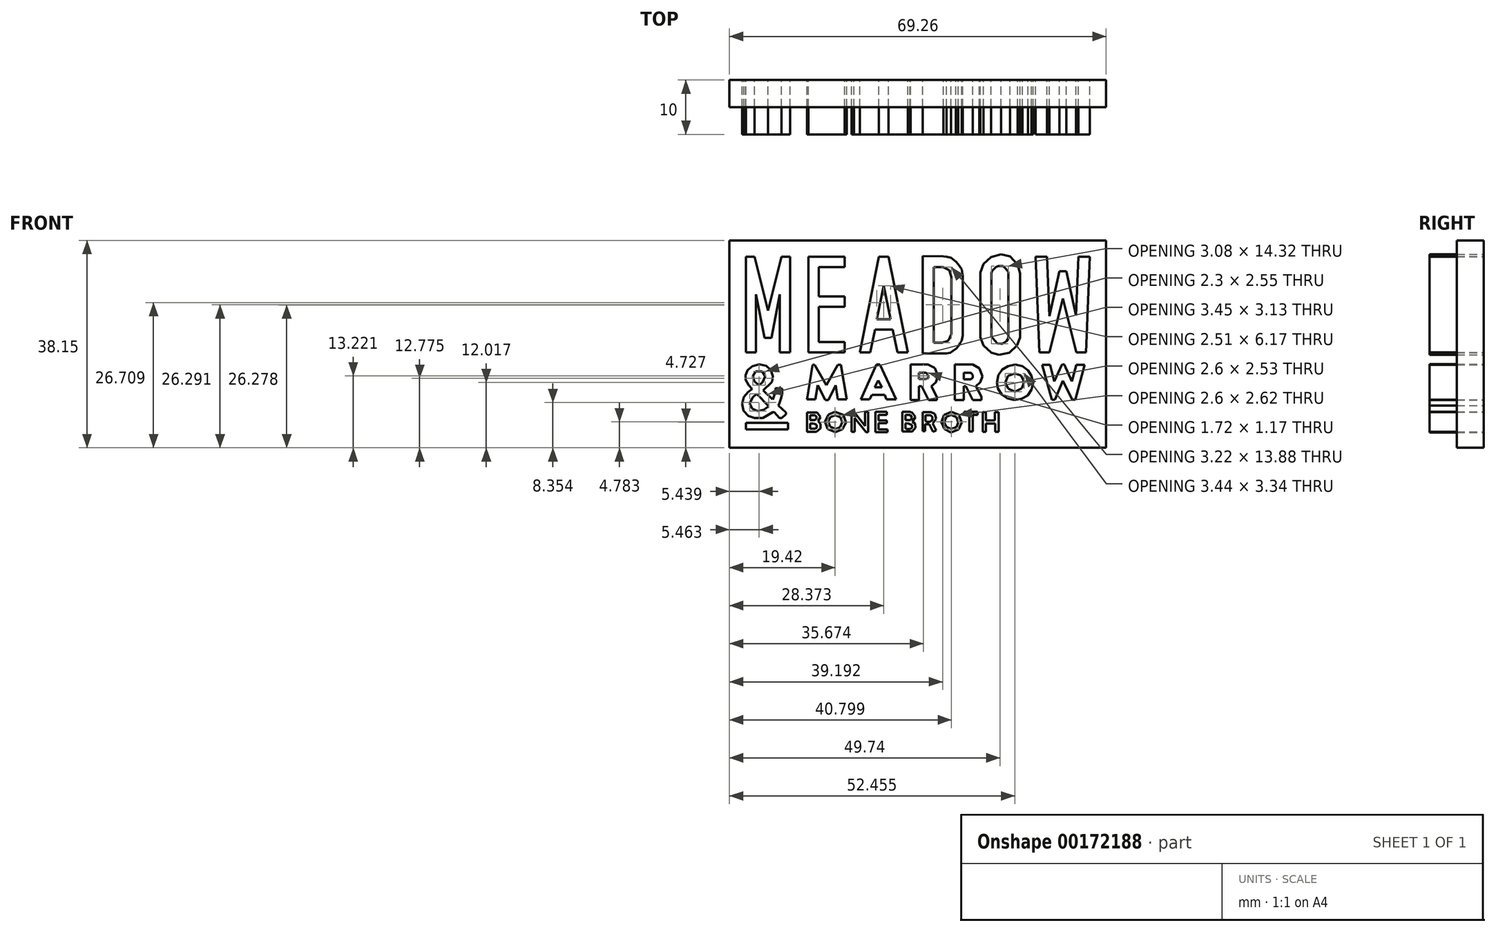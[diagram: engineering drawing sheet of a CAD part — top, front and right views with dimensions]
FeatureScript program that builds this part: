
annotation { "Feature Type Name" : "Feature", "Feature Type Description" : "" }
export const myFeature = defineFeature(function(context is Context, id is Id, definition is map)
    precondition{}
    {
        {
            var Q0;
            Q0=qCreatedBy(makeId("Front.planeOp"),FACE);
            var sketch = newSketch(context, id + "F0", { "sketchPlane" : qUnion([Q0])});
            skLineSegment(sketch, "E0", {"start": v(-7.57, -8.05) * mm, "end": v(-6.9, -6.6) * mm});
            skLineSegment(sketch, "E1", {"start": v(-6.9, -6.6) * mm, "end": v(-6.9, -6.6) * mm});
            skLineSegment(sketch, "E2", {"start": v(-6.9, -6.6) * mm, "end": v(-6.23, -8.05) * mm});
            skLineSegment(sketch, "E3", {"start": v(-6.23, -8.05) * mm, "end": v(-7.57, -8.05) * mm});
            skLineSegment(sketch, "E4", {"start": v(-31.63, -15.97) * mm, "end": v(-23.85, -15.97) * mm});
            skLineSegment(sketch, "E5", {"start": v(-23.85, -15.97) * mm, "end": v(-23.85, -14.73) * mm});
            skLineSegment(sketch, "E6", {"start": v(-23.85, -14.73) * mm, "end": v(-31.63, -14.73) * mm});
            skLineSegment(sketch, "E7", {"start": v(-31.63, -14.73) * mm, "end": v(-31.63, -15.97) * mm});
            skLineSegment(sketch, "E8", {"start": v(-5.38, 15.8) * mm, "end": v(-7.14, 15.8) * mm});
            skLineSegment(sketch, "E9", {"start": v(-7.14, 15.8) * mm, "end": v(-10.66, -1.8) * mm});
            skLineSegment(sketch, "E10", {"start": v(-10.66, -1.8) * mm, "end": v(-8.75, -1.8) * mm});
            skLineSegment(sketch, "E11", {"start": v(-8.75, -1.8) * mm, "end": v(-7.9, 2.38) * mm});
            skLineSegment(sketch, "E12", {"start": v(-7.9, 2.38) * mm, "end": v(-4.62, 2.38) * mm});
            skLineSegment(sketch, "E13", {"start": v(-4.62, 2.38) * mm, "end": v(-3.76, -1.8) * mm});
            skLineSegment(sketch, "E14", {"start": v(-3.76, -1.8) * mm, "end": v(-1.86, -1.8) * mm});
            skLineSegment(sketch, "E15", {"start": v(-1.86, -1.8) * mm, "end": v(-5.38, 15.8) * mm});
            skLineSegment(sketch, "E16", {"start": v(-7.51, 4.28) * mm, "end": v(-6.26, 10.44) * mm});
            skLineSegment(sketch, "E17", {"start": v(-6.26, 10.44) * mm, "end": v(-5, 4.28) * mm});
            skLineSegment(sketch, "E18", {"start": v(-5, 4.28) * mm, "end": v(-7.51, 4.28) * mm});
            skLineSegment(sketch, "E19", {"start": v(29.55, 15.8) * mm, "end": v(29.08, 5) * mm});
            skLineSegment(sketch, "E20", {"start": v(29.08, 5) * mm, "end": v(27.32, 13.16) * mm});
            skLineSegment(sketch, "E21", {"start": v(27.32, 13.16) * mm, "end": v(26.02, 13.16) * mm});
            skLineSegment(sketch, "E22", {"start": v(26.02, 13.16) * mm, "end": v(24.23, 4.9) * mm});
            skLineSegment(sketch, "E23", {"start": v(24.23, 4.9) * mm, "end": v(23.79, 15.8) * mm});
            skLineSegment(sketch, "E24", {"start": v(23.79, 15.8) * mm, "end": v(21.69, 15.8) * mm});
            skLineSegment(sketch, "E25", {"start": v(21.69, 15.8) * mm, "end": v(22.38, -1.79) * mm});
            skLineSegment(sketch, "E26", {"start": v(22.38, -1.79) * mm, "end": v(24.19, -1.79) * mm});
            skLineSegment(sketch, "E27", {"start": v(24.19, -1.79) * mm, "end": v(26.68, 8.1) * mm});
            skLineSegment(sketch, "E28", {"start": v(26.68, 8.1) * mm, "end": v(29.13, -1.79) * mm});
            skLineSegment(sketch, "E29", {"start": v(29.13, -1.79) * mm, "end": v(30.94, -1.79) * mm});
            skLineSegment(sketch, "E30", {"start": v(30.94, -1.79) * mm, "end": v(31.63, 15.8) * mm});
            skLineSegment(sketch, "E31", {"start": v(31.63, 15.8) * mm, "end": v(29.55, 15.8) * mm});
            skLineSegment(sketch, "E32", {"start": v(-13.46, 0.1) * mm, "end": v(-18.21, 0.1) * mm});
            skLineSegment(sketch, "E33", {"start": v(-18.21, 0.1) * mm, "end": v(-18.21, 6.59) * mm});
            skLineSegment(sketch, "E34", {"start": v(-18.21, 6.59) * mm, "end": v(-13.46, 6.59) * mm});
            skLineSegment(sketch, "E35", {"start": v(-13.46, 6.59) * mm, "end": v(-13.46, 8.48) * mm});
            skLineSegment(sketch, "E36", {"start": v(-13.46, 8.48) * mm, "end": v(-18.21, 8.48) * mm});
            skLineSegment(sketch, "E37", {"start": v(-18.21, 8.48) * mm, "end": v(-18.21, 13.9) * mm});
            skLineSegment(sketch, "E38", {"start": v(-18.21, 13.9) * mm, "end": v(-13.46, 13.9) * mm});
            skLineSegment(sketch, "E39", {"start": v(-13.46, 13.9) * mm, "end": v(-13.46, 15.8) * mm});
            skLineSegment(sketch, "E40", {"start": v(-13.46, 15.8) * mm, "end": v(-20.1, 15.8) * mm});
            skLineSegment(sketch, "E41", {"start": v(-20.1, 15.8) * mm, "end": v(-20.1, -1.8) * mm});
            skLineSegment(sketch, "E42", {"start": v(-20.1, -1.8) * mm, "end": v(-13.46, -1.8) * mm});
            skLineSegment(sketch, "E43", {"start": v(-13.46, -1.8) * mm, "end": v(-13.46, 0.1) * mm});
            skLineSegment(sketch, "E44", {"start": v(-27.56, 5.91) * mm, "end": v(-30.01, 15.8) * mm});
            skLineSegment(sketch, "E45", {"start": v(-30.01, 15.8) * mm, "end": v(-31.63, 15.8) * mm});
            skLineSegment(sketch, "E46", {"start": v(-31.63, 15.8) * mm, "end": v(-31.63, -1.8) * mm});
            skLineSegment(sketch, "E47", {"start": v(-31.63, -1.8) * mm, "end": v(-29.74, -1.8) * mm});
            skLineSegment(sketch, "E48", {"start": v(-29.74, -1.8) * mm, "end": v(-29.74, 8.85) * mm});
            skLineSegment(sketch, "E49", {"start": v(-29.74, 8.85) * mm, "end": v(-28.2, 0.84) * mm});
            skLineSegment(sketch, "E50", {"start": v(-28.2, 0.84) * mm, "end": v(-26.9, 0.84) * mm});
            skLineSegment(sketch, "E51", {"start": v(-26.9, 0.84) * mm, "end": v(-25.36, 8.85) * mm});
            skLineSegment(sketch, "E52", {"start": v(-25.36, 8.85) * mm, "end": v(-25.36, -1.8) * mm});
            skLineSegment(sketch, "E53", {"start": v(-25.36, -1.8) * mm, "end": v(-23.47, -1.8) * mm});
            skLineSegment(sketch, "E54", {"start": v(-23.47, -1.8) * mm, "end": v(-23.47, 15.8) * mm});
            skLineSegment(sketch, "E55", {"start": v(-23.47, 15.8) * mm, "end": v(-25.06, 15.8) * mm});
            skLineSegment(sketch, "E56", {"start": v(-25.06, 15.8) * mm, "end": v(-27.56, 5.91) * mm});
            skSolve(sketch);
        }
        {
            var Q0;
            Q0=qCreatedBy(makeId("Front.planeOp"),FACE);
            var sketch = newSketch(context, id + "F1", { "sketchPlane" : qUnion([Q0])});
            skLineSegment(sketch, "E57", {"start": v(0.89, 15.9) * mm, "end": v(0.89, -1.98) * mm});
            skLineSegment(sketch, "E58", {"start": v(0.89, -1.98) * mm, "end": v(5.3, -1.98) * mm});
            skLineSegment(sketch, "E59", {"start": v(5.3, -1.98) * mm, "end": v(5.97, -1.83) * mm});
            skLineSegment(sketch, "E60", {"start": v(5.97, -1.83) * mm, "end": v(6.45, -1.51) * mm});
            skLineSegment(sketch, "E61", {"start": v(6.45, -1.51) * mm, "end": v(7.04, -1.1) * mm});
            skLineSegment(sketch, "E62", {"start": v(7.04, -1.1) * mm, "end": v(7.52, -0.56) * mm});
            skLineSegment(sketch, "E63", {"start": v(7.52, -0.56) * mm, "end": v(7.81, 0) * mm});
            skLineSegment(sketch, "E64", {"start": v(7.81, 0) * mm, "end": v(8.06, 0.36) * mm});
            skLineSegment(sketch, "E65", {"start": v(8.06, 0.36) * mm, "end": v(8.21, 1) * mm});
            skLineSegment(sketch, "E66", {"start": v(8.21, 1) * mm, "end": v(8.29, 1.32) * mm});
            skLineSegment(sketch, "E67", {"start": v(8.29, 1.32) * mm, "end": v(8.29, 12.23) * mm});
            skLineSegment(sketch, "E68", {"start": v(8.29, 12.23) * mm, "end": v(8.1, 13.5) * mm});
            skLineSegment(sketch, "E69", {"start": v(8.1, 13.5) * mm, "end": v(7.45, 14.4) * mm});
            skLineSegment(sketch, "E70", {"start": v(7.45, 14.4) * mm, "end": v(6.99, 14.94) * mm});
            skLineSegment(sketch, "E71", {"start": v(6.99, 14.94) * mm, "end": v(6.1, 15.58) * mm});
            skLineSegment(sketch, "E72", {"start": v(6.1, 15.58) * mm, "end": v(5.3, 15.8) * mm});
            skLineSegment(sketch, "E73", {"start": v(5.3, 15.8) * mm, "end": v(4.74, 15.88) * mm});
            skLineSegment(sketch, "E74", {"start": v(4.74, 15.88) * mm, "end": v(0.89, 15.9) * mm});
            skLineSegment(sketch, "E75", {"start": v(2.95, 13.87) * mm, "end": v(2.95, 0) * mm});
            skLineSegment(sketch, "E76", {"start": v(2.95, 0) * mm, "end": v(4.47, 0) * mm});
            skLineSegment(sketch, "E77", {"start": v(4.47, 0) * mm, "end": v(5.48, 0.3) * mm});
            skLineSegment(sketch, "E78", {"start": v(5.48, 0.3) * mm, "end": v(5.73, 0.54) * mm});
            skLineSegment(sketch, "E79", {"start": v(5.73, 0.54) * mm, "end": v(6.14, 1.46) * mm});
            skLineSegment(sketch, "E80", {"start": v(6.14, 1.46) * mm, "end": v(6.17, 1.54) * mm});
            skLineSegment(sketch, "E81", {"start": v(6.17, 1.54) * mm, "end": v(6.17, 12.02) * mm});
            skLineSegment(sketch, "E82", {"start": v(6.17, 12.02) * mm, "end": v(5.8, 13.32) * mm});
            skLineSegment(sketch, "E83", {"start": v(5.8, 13.32) * mm, "end": v(4.63, 13.88) * mm});
            skLineSegment(sketch, "E84", {"start": v(4.63, 13.88) * mm, "end": v(2.95, 13.87) * mm});
            skLineSegment(sketch, "E85", {"start": v(13.57, 12.8) * mm, "end": v(13.57, 1.13) * mm});
            skLineSegment(sketch, "E86", {"start": v(13.57, 1.13) * mm, "end": v(14.15, 0.34) * mm});
            skLineSegment(sketch, "E87", {"start": v(14.15, 0.34) * mm, "end": v(14.59, -0.14) * mm});
            skLineSegment(sketch, "E88", {"start": v(14.59, -0.14) * mm, "end": v(15.25, -0.23) * mm});
            skLineSegment(sketch, "E89", {"start": v(15.25, -0.23) * mm, "end": v(15.52, -0.23) * mm});
            skLineSegment(sketch, "E90", {"start": v(15.52, -0.23) * mm, "end": v(15.91, 0) * mm});
            skLineSegment(sketch, "E91", {"start": v(15.91, 0) * mm, "end": v(16.35, 0.32) * mm});
            skLineSegment(sketch, "E92", {"start": v(16.35, 0.32) * mm, "end": v(16.65, 0.8) * mm});
            skLineSegment(sketch, "E93", {"start": v(16.65, 0.8) * mm, "end": v(16.65, 1.05) * mm});
            skLineSegment(sketch, "E94", {"start": v(16.65, 1.05) * mm, "end": v(16.65, 13) * mm});
            skLineSegment(sketch, "E95", {"start": v(16.65, 13) * mm, "end": v(16.16, 13.65) * mm});
            skLineSegment(sketch, "E96", {"start": v(16.16, 13.65) * mm, "end": v(15.67, 14.09) * mm});
            skLineSegment(sketch, "E97", {"start": v(15.67, 14.09) * mm, "end": v(14.82, 14.09) * mm});
            skLineSegment(sketch, "E98", {"start": v(14.82, 14.09) * mm, "end": v(14.36, 13.86) * mm});
            skLineSegment(sketch, "E99", {"start": v(14.36, 13.86) * mm, "end": v(13.95, 13.51) * mm});
            skLineSegment(sketch, "E100", {"start": v(13.95, 13.51) * mm, "end": v(13.67, 13.22) * mm});
            skLineSegment(sketch, "E101", {"start": v(13.67, 13.22) * mm, "end": v(13.57, 12.8) * mm});
            skLineSegment(sketch, "E102", {"start": v(11.5, 12.88) * mm, "end": v(11.5, 1.03) * mm});
            skLineSegment(sketch, "E103", {"start": v(11.5, 1.03) * mm, "end": v(12.07, -0.53) * mm});
            skLineSegment(sketch, "E104", {"start": v(12.07, -0.53) * mm, "end": v(13.53, -1.87) * mm});
            skLineSegment(sketch, "E105", {"start": v(13.53, -1.87) * mm, "end": v(14.96, -2.25) * mm});
            skLineSegment(sketch, "E106", {"start": v(14.96, -2.25) * mm, "end": v(16.81, -1.86) * mm});
            skLineSegment(sketch, "E107", {"start": v(16.81, -1.86) * mm, "end": v(18.23, -0.53) * mm});
            skLineSegment(sketch, "E108", {"start": v(18.23, -0.53) * mm, "end": v(18.82, 0.93) * mm});
            skLineSegment(sketch, "E109", {"start": v(18.82, 0.93) * mm, "end": v(18.82, 12.77) * mm});
            skLineSegment(sketch, "E110", {"start": v(18.82, 12.77) * mm, "end": v(18.37, 14.36) * mm});
            skLineSegment(sketch, "E111", {"start": v(18.37, 14.36) * mm, "end": v(16.98, 15.88) * mm});
            skLineSegment(sketch, "E112", {"start": v(16.98, 15.88) * mm, "end": v(15.33, 16.22) * mm});
            skLineSegment(sketch, "E113", {"start": v(15.33, 16.22) * mm, "end": v(13.48, 15.74) * mm});
            skLineSegment(sketch, "E114", {"start": v(13.48, 15.74) * mm, "end": v(12.07, 14.46) * mm});
            skLineSegment(sketch, "E115", {"start": v(12.07, 14.46) * mm, "end": v(11.5, 12.88) * mm});
            skLineSegment(sketch, "E116", {"start": v(-29.27, -7.85) * mm, "end": v(-28.57, -7.34) * mm});
            skLineSegment(sketch, "E117", {"start": v(-28.57, -7.34) * mm, "end": v(-28.04, -6.15) * mm});
            skLineSegment(sketch, "E118", {"start": v(-28.04, -6.15) * mm, "end": v(-28.61, -5.3) * mm});
            skLineSegment(sketch, "E119", {"start": v(-28.61, -5.3) * mm, "end": v(-29.8, -5.3) * mm});
            skLineSegment(sketch, "E120", {"start": v(-29.8, -5.3) * mm, "end": v(-30.34, -6.2) * mm});
            skLineSegment(sketch, "E121", {"start": v(-30.34, -6.2) * mm, "end": v(-30.06, -7.08) * mm});
            skLineSegment(sketch, "E122", {"start": v(-30.06, -7.08) * mm, "end": v(-29.27, -7.85) * mm});
            skLineSegment(sketch, "E123", {"start": v(-26.73, -10.45) * mm, "end": v(-28.4, -8.8) * mm});
            skLineSegment(sketch, "E124", {"start": v(-28.4, -8.8) * mm, "end": v(-26.92, -7.3) * mm});
            skLineSegment(sketch, "E125", {"start": v(-26.92, -7.3) * mm, "end": v(-26.77, -7.1) * mm});
            skLineSegment(sketch, "E126", {"start": v(-26.77, -7.1) * mm, "end": v(-26.64, -6.18) * mm});
            skLineSegment(sketch, "E127", {"start": v(-26.64, -6.18) * mm, "end": v(-27.04, -5.05) * mm});
            skLineSegment(sketch, "E128", {"start": v(-27.04, -5.05) * mm, "end": v(-27.85, -4.3) * mm});
            skLineSegment(sketch, "E129", {"start": v(-27.85, -4.3) * mm, "end": v(-28.98, -4.02) * mm});
            skLineSegment(sketch, "E130", {"start": v(-28.98, -4.02) * mm, "end": v(-29.27, -4.02) * mm});
            skLineSegment(sketch, "E131", {"start": v(-29.27, -4.02) * mm, "end": v(-30.42, -4.31) * mm});
            skLineSegment(sketch, "E132", {"start": v(-30.42, -4.31) * mm, "end": v(-31.27, -5.05) * mm});
            skLineSegment(sketch, "E133", {"start": v(-31.27, -5.05) * mm, "end": v(-31.67, -6) * mm});
            skLineSegment(sketch, "E134", {"start": v(-31.67, -6) * mm, "end": v(-31.67, -6.83) * mm});
            skLineSegment(sketch, "E135", {"start": v(-31.67, -6.83) * mm, "end": v(-31.1, -7.85) * mm});
            skLineSegment(sketch, "E136", {"start": v(-31.1, -7.85) * mm, "end": v(-30.45, -8.53) * mm});
            skLineSegment(sketch, "E137", {"start": v(-30.45, -8.53) * mm, "end": v(-31.22, -9.1) * mm});
            skLineSegment(sketch, "E138", {"start": v(-31.22, -9.1) * mm, "end": v(-31.99, -9.96) * mm});
            skLineSegment(sketch, "E139", {"start": v(-31.99, -9.96) * mm, "end": v(-32.29, -11.25) * mm});
            skLineSegment(sketch, "E140", {"start": v(-32.29, -11.25) * mm, "end": v(-32.04, -12.5) * mm});
            skLineSegment(sketch, "E141", {"start": v(-32.04, -12.5) * mm, "end": v(-31.18, -13.46) * mm});
            skLineSegment(sketch, "E142", {"start": v(-31.18, -13.46) * mm, "end": v(-30, -13.87) * mm});
            skLineSegment(sketch, "E143", {"start": v(-30, -13.87) * mm, "end": v(-28.53, -13.87) * mm});
            skLineSegment(sketch, "E144", {"start": v(-28.53, -13.87) * mm, "end": v(-26.66, -12.8) * mm});
            skLineSegment(sketch, "E145", {"start": v(-26.66, -12.8) * mm, "end": v(-26.42, -12.8) * mm});
            skLineSegment(sketch, "E146", {"start": v(-26.42, -12.8) * mm, "end": v(-25.45, -13.85) * mm});
            skLineSegment(sketch, "E147", {"start": v(-25.45, -13.85) * mm, "end": v(-24.98, -13.85) * mm});
            skLineSegment(sketch, "E148", {"start": v(-24.98, -13.85) * mm, "end": v(-24.27, -13.17) * mm});
            skLineSegment(sketch, "E149", {"start": v(-24.27, -13.17) * mm, "end": v(-24.27, -12.82) * mm});
            skLineSegment(sketch, "E150", {"start": v(-24.27, -12.82) * mm, "end": v(-25.61, -11.57) * mm});
            skLineSegment(sketch, "E151", {"start": v(-25.61, -11.57) * mm, "end": v(-25.45, -11.1) * mm});
            skLineSegment(sketch, "E152", {"start": v(-25.45, -11.1) * mm, "end": v(-25.13, -10.2) * mm});
            skLineSegment(sketch, "E153", {"start": v(-25.13, -10.2) * mm, "end": v(-24.93, -9.35) * mm});
            skLineSegment(sketch, "E154", {"start": v(-24.93, -9.35) * mm, "end": v(-24.93, -8.43) * mm});
            skLineSegment(sketch, "E155", {"start": v(-24.93, -8.43) * mm, "end": v(-26.17, -8.33) * mm});
            skLineSegment(sketch, "E156", {"start": v(-26.17, -8.33) * mm, "end": v(-26.22, -9.01) * mm});
            skLineSegment(sketch, "E157", {"start": v(-26.22, -9.01) * mm, "end": v(-26.33, -9.49) * mm});
            skLineSegment(sketch, "E158", {"start": v(-26.33, -9.49) * mm, "end": v(-26.5, -10.08) * mm});
            skLineSegment(sketch, "E159", {"start": v(-26.5, -10.08) * mm, "end": v(-26.73, -10.45) * mm});
            skLineSegment(sketch, "E160", {"start": v(-29.62, -9.43) * mm, "end": v(-30.37, -10.08) * mm});
            skLineSegment(sketch, "E161", {"start": v(-30.37, -10.08) * mm, "end": v(-30.9, -11.18) * mm});
            skLineSegment(sketch, "E162", {"start": v(-30.9, -11.18) * mm, "end": v(-30.45, -12.13) * mm});
            skLineSegment(sketch, "E163", {"start": v(-30.45, -12.13) * mm, "end": v(-29.43, -12.56) * mm});
            skLineSegment(sketch, "E164", {"start": v(-29.43, -12.56) * mm, "end": v(-28.29, -12.34) * mm});
            skLineSegment(sketch, "E165", {"start": v(-28.29, -12.34) * mm, "end": v(-27.44, -11.7) * mm});
            skLineSegment(sketch, "E166", {"start": v(-27.44, -11.7) * mm, "end": v(-29.62, -9.43) * mm});
            skLineSegment(sketch, "E167", {"start": v(-20.4, -10.45) * mm, "end": v(-19.33, -4.07) * mm});
            skLineSegment(sketch, "E168", {"start": v(-19.33, -4.07) * mm, "end": v(-19, -4.07) * mm});
            skLineSegment(sketch, "E169", {"start": v(-19, -4.07) * mm, "end": v(-16.8, -7.85) * mm});
            skLineSegment(sketch, "E170", {"start": v(-16.8, -7.85) * mm, "end": v(-14.71, -4.08) * mm});
            skLineSegment(sketch, "E171", {"start": v(-14.71, -4.08) * mm, "end": v(-14.17, -4.08) * mm});
            skLineSegment(sketch, "E172", {"start": v(-14.17, -4.08) * mm, "end": v(-13.04, -10.45) * mm});
            skLineSegment(sketch, "E173", {"start": v(-13.04, -10.45) * mm, "end": v(-14.7, -10.45) * mm});
            skLineSegment(sketch, "E174", {"start": v(-14.7, -10.45) * mm, "end": v(-15.1, -7.85) * mm});
            skLineSegment(sketch, "E175", {"start": v(-15.1, -7.85) * mm, "end": v(-16.44, -10.54) * mm});
            skLineSegment(sketch, "E176", {"start": v(-16.44, -10.54) * mm, "end": v(-17.01, -10.54) * mm});
            skLineSegment(sketch, "E177", {"start": v(-17.01, -10.54) * mm, "end": v(-18.43, -7.85) * mm});
            skLineSegment(sketch, "E178", {"start": v(-18.43, -7.85) * mm, "end": v(-18.83, -10.45) * mm});
            skLineSegment(sketch, "E179", {"start": v(-18.83, -10.45) * mm, "end": v(-20.4, -10.45) * mm});
            skLineSegment(sketch, "E180", {"start": v(-8.44, -9.6) * mm, "end": v(-6.11, -9.6) * mm});
            skLineSegment(sketch, "E181", {"start": v(-6.11, -9.6) * mm, "end": v(-5.76, -10.45) * mm});
            skLineSegment(sketch, "E182", {"start": v(-5.76, -10.45) * mm, "end": v(-4, -10.45) * mm});
            skLineSegment(sketch, "E183", {"start": v(-4, -10.45) * mm, "end": v(-7, -4.02) * mm});
            skLineSegment(sketch, "E184", {"start": v(-7, -4.02) * mm, "end": v(-7.58, -4.02) * mm});
            skLineSegment(sketch, "E185", {"start": v(-7.58, -4.02) * mm, "end": v(-10.48, -10.45) * mm});
            skLineSegment(sketch, "E186", {"start": v(-10.48, -10.45) * mm, "end": v(-8.9, -10.45) * mm});
            skLineSegment(sketch, "E187", {"start": v(-8.9, -10.45) * mm, "end": v(-8.44, -9.6) * mm});
            skLineSegment(sketch, "E188", {"start": v(-7.3, -6.92) * mm, "end": v(-7.9, -8.22) * mm});
            skLineSegment(sketch, "E189", {"start": v(-7.9, -8.22) * mm, "end": v(-6.62, -8.22) * mm});
            skLineSegment(sketch, "E190", {"start": v(-6.62, -8.22) * mm, "end": v(-7.3, -6.92) * mm});
            skLineSegment(sketch, "E191", {"start": v(-1.33, -4.04) * mm, "end": v(-1.33, -10.54) * mm});
            skLineSegment(sketch, "E192", {"start": v(-1.33, -10.54) * mm, "end": v(0.18, -10.54) * mm});
            skLineSegment(sketch, "E193", {"start": v(0.18, -10.54) * mm, "end": v(0.18, -8.03) * mm});
            skLineSegment(sketch, "E194", {"start": v(0.18, -8.03) * mm, "end": v(0.7, -8.03) * mm});
            skLineSegment(sketch, "E195", {"start": v(0.7, -8.03) * mm, "end": v(1.96, -10.54) * mm});
            skLineSegment(sketch, "E196", {"start": v(1.96, -10.54) * mm, "end": v(3.5, -10.54) * mm});
            skLineSegment(sketch, "E197", {"start": v(3.5, -10.54) * mm, "end": v(3.5, -10.01) * mm});
            skLineSegment(sketch, "E198", {"start": v(3.5, -10.01) * mm, "end": v(2.46, -8.03) * mm});
            skLineSegment(sketch, "E199", {"start": v(2.46, -8.03) * mm, "end": v(3.3, -7.31) * mm});
            skLineSegment(sketch, "E200", {"start": v(3.3, -7.31) * mm, "end": v(3.71, -6.13) * mm});
            skLineSegment(sketch, "E201", {"start": v(3.71, -6.13) * mm, "end": v(3.13, -4.67) * mm});
            skLineSegment(sketch, "E202", {"start": v(3.13, -4.67) * mm, "end": v(1.83, -4.04) * mm});
            skLineSegment(sketch, "E203", {"start": v(1.83, -4.04) * mm, "end": v(-1.33, -4.04) * mm});
            skLineSegment(sketch, "E204", {"start": v(0.18, -5.55) * mm, "end": v(0.18, -6.71) * mm});
            skLineSegment(sketch, "E205", {"start": v(0.18, -6.71) * mm, "end": v(1.48, -6.71) * mm});
            skLineSegment(sketch, "E206", {"start": v(1.48, -6.71) * mm, "end": v(1.9, -6.54) * mm});
            skLineSegment(sketch, "E207", {"start": v(1.9, -6.54) * mm, "end": v(1.9, -5.97) * mm});
            skLineSegment(sketch, "E208", {"start": v(1.9, -5.97) * mm, "end": v(1.55, -5.55) * mm});
            skLineSegment(sketch, "E209", {"start": v(1.55, -5.55) * mm, "end": v(0.18, -5.55) * mm});
            skLineSegment(sketch, "E210", {"start": v(8.44, -5.55) * mm, "end": v(8.44, -6.72) * mm});
            skPoint(sketch, "E210.endSnap0", {"position": v(3.5, -6.72) * mm});
            skLineSegment(sketch, "E211", {"start": v(8.44, -6.72) * mm, "end": v(9.67, -6.72) * mm});
            skLineSegment(sketch, "E212", {"start": v(9.67, -6.72) * mm, "end": v(10.1, -6.5) * mm});
            skLineSegment(sketch, "E213", {"start": v(10.1, -6.5) * mm, "end": v(10.1, -5.97) * mm});
            skLineSegment(sketch, "E214", {"start": v(10.1, -5.97) * mm, "end": v(9.78, -5.55) * mm});
            skLineSegment(sketch, "E215", {"start": v(9.78, -5.55) * mm, "end": v(8.44, -5.55) * mm});
            skLineSegment(sketch, "E216", {"start": v(6.82, -4.04) * mm, "end": v(6.82, -10.54) * mm});
            skLineSegment(sketch, "E217", {"start": v(6.82, -10.54) * mm, "end": v(8.44, -10.54) * mm});
            skLineSegment(sketch, "E218", {"start": v(8.44, -10.54) * mm, "end": v(8.44, -8.03) * mm});
            skLineSegment(sketch, "E219", {"start": v(8.44, -8.03) * mm, "end": v(8.86, -8.03) * mm});
            skLineSegment(sketch, "E220", {"start": v(8.86, -8.03) * mm, "end": v(10.1, -10.54) * mm});
            skLineSegment(sketch, "E221", {"start": v(10.1, -10.54) * mm, "end": v(11.7, -10.54) * mm});
            skLineSegment(sketch, "E222", {"start": v(11.7, -10.54) * mm, "end": v(11.7, -9.95) * mm});
            skLineSegment(sketch, "E223", {"start": v(11.7, -9.95) * mm, "end": v(10.66, -8.03) * mm});
            skLineSegment(sketch, "E224", {"start": v(10.66, -8.03) * mm, "end": v(11.5, -7.24) * mm});
            skLineSegment(sketch, "E225", {"start": v(11.5, -7.24) * mm, "end": v(11.88, -6.14) * mm});
            skLineSegment(sketch, "E226", {"start": v(11.88, -6.14) * mm, "end": v(11.32, -4.74) * mm});
            skLineSegment(sketch, "E227", {"start": v(11.32, -4.74) * mm, "end": v(10.1, -4.04) * mm});
            skLineSegment(sketch, "E228", {"start": v(10.1, -4.04) * mm, "end": v(6.82, -4.04) * mm});
            skLineSegment(sketch, "E229", {"start": v(16.56, -6.1) * mm, "end": v(17.84, -5.66) * mm});
            skLineSegment(sketch, "E230", {"start": v(17.84, -5.66) * mm, "end": v(18.98, -6.06) * mm});
            skLineSegment(sketch, "E231", {"start": v(18.98, -6.06) * mm, "end": v(19.54, -7.23) * mm});
            skLineSegment(sketch, "E232", {"start": v(19.54, -7.23) * mm, "end": v(19.14, -8.4) * mm});
            skLineSegment(sketch, "E233", {"start": v(19.14, -8.4) * mm, "end": v(17.88, -9) * mm});
            skLineSegment(sketch, "E234", {"start": v(17.88, -9) * mm, "end": v(16.63, -8.49) * mm});
            skLineSegment(sketch, "E235", {"start": v(16.63, -8.49) * mm, "end": v(16.1, -7.4) * mm});
            skLineSegment(sketch, "E236", {"start": v(16.1, -7.4) * mm, "end": v(16.56, -6.1) * mm});
            skLineSegment(sketch, "E237", {"start": v(15.52, -4.98) * mm, "end": v(14.83, -5.97) * mm});
            skLineSegment(sketch, "E238", {"start": v(14.83, -5.97) * mm, "end": v(14.54, -7.37) * mm});
            skLineSegment(sketch, "E239", {"start": v(14.54, -7.37) * mm, "end": v(14.73, -8.46) * mm});
            skLineSegment(sketch, "E240", {"start": v(14.73, -8.46) * mm, "end": v(15.46, -9.53) * mm});
            skLineSegment(sketch, "E241", {"start": v(15.46, -9.53) * mm, "end": v(16.45, -10.23) * mm});
            skLineSegment(sketch, "E242", {"start": v(16.45, -10.23) * mm, "end": v(17.72, -10.56) * mm});
            skLineSegment(sketch, "E243", {"start": v(17.72, -10.56) * mm, "end": v(19.12, -10.27) * mm});
            skLineSegment(sketch, "E244", {"start": v(19.12, -10.27) * mm, "end": v(20.2, -9.75) * mm});
            skLineSegment(sketch, "E245", {"start": v(20.2, -9.75) * mm, "end": v(20.92, -8.67) * mm});
            skLineSegment(sketch, "E246", {"start": v(20.92, -8.67) * mm, "end": v(21.24, -7.36) * mm});
            skLineSegment(sketch, "E247", {"start": v(21.24, -7.36) * mm, "end": v(20.93, -6.1) * mm});
            skLineSegment(sketch, "E248", {"start": v(20.93, -6.1) * mm, "end": v(20.27, -5.07) * mm});
            skLineSegment(sketch, "E249", {"start": v(20.27, -5.07) * mm, "end": v(19.26, -4.3) * mm});
            skLineSegment(sketch, "E250", {"start": v(19.26, -4.3) * mm, "end": v(17.95, -4.04) * mm});
            skLineSegment(sketch, "E251", {"start": v(17.95, -4.04) * mm, "end": v(16.56, -4.3) * mm});
            skLineSegment(sketch, "E252", {"start": v(16.56, -4.3) * mm, "end": v(15.52, -4.98) * mm});
            skLineSegment(sketch, "E253", {"start": v(22.9, -4.08) * mm, "end": v(24.31, -4.08) * mm});
            skLineSegment(sketch, "E254", {"start": v(24.31, -4.08) * mm, "end": v(25.12, -7.15) * mm});
            skLineSegment(sketch, "E255", {"start": v(25.12, -7.15) * mm, "end": v(26.47, -4.1) * mm});
            skLineSegment(sketch, "E256", {"start": v(26.47, -4.1) * mm, "end": v(26.67, -3.94) * mm});
            skLineSegment(sketch, "E257", {"start": v(26.67, -3.94) * mm, "end": v(26.94, -4.02) * mm});
            skPoint(sketch, "E257.endSnap0", {"position": v(26.57, -4.02) * mm});
            skLineSegment(sketch, "E258", {"start": v(26.94, -4.02) * mm, "end": v(28.31, -7.15) * mm});
            skLineSegment(sketch, "E259", {"start": v(28.31, -7.15) * mm, "end": v(29.17, -4.1) * mm});
            skLineSegment(sketch, "E260", {"start": v(29.17, -4.1) * mm, "end": v(30.7, -4.1) * mm});
            skLineSegment(sketch, "E261", {"start": v(30.7, -4.1) * mm, "end": v(28.94, -10.5) * mm});
            skLineSegment(sketch, "E262", {"start": v(28.94, -10.5) * mm, "end": v(28.43, -10.5) * mm});
            skLineSegment(sketch, "E263", {"start": v(28.43, -10.5) * mm, "end": v(26.67, -7) * mm});
            skLineSegment(sketch, "E264", {"start": v(26.67, -7) * mm, "end": v(25.2, -10.5) * mm});
            skLineSegment(sketch, "E265", {"start": v(25.2, -10.5) * mm, "end": v(24.67, -10.5) * mm});
            skLineSegment(sketch, "E266", {"start": v(24.67, -10.5) * mm, "end": v(22.9, -4.08) * mm});
            skLineSegment(sketch, "E267", {"start": v(-20.4, -12.82) * mm, "end": v(-20.4, -16.37) * mm});
            skLineSegment(sketch, "E268", {"start": v(-20.4, -16.37) * mm, "end": v(-18.66, -16.37) * mm});
            skLineSegment(sketch, "E269", {"start": v(-18.66, -16.37) * mm, "end": v(-17.9, -15.76) * mm});
            skLineSegment(sketch, "E270", {"start": v(-17.9, -15.76) * mm, "end": v(-17.9, -14.93) * mm});
            skLineSegment(sketch, "E271", {"start": v(-17.9, -14.93) * mm, "end": v(-18.32, -14.42) * mm});
            skLineSegment(sketch, "E272", {"start": v(-18.32, -14.42) * mm, "end": v(-17.9, -13.64) * mm});
            skLineSegment(sketch, "E273", {"start": v(-17.9, -13.64) * mm, "end": v(-18.56, -12.82) * mm});
            skLineSegment(sketch, "E274", {"start": v(-18.56, -12.82) * mm, "end": v(-20.4, -12.82) * mm});
            skLineSegment(sketch, "E275", {"start": v(-19.79, -13.36) * mm, "end": v(-19.79, -14.22) * mm});
            skLineSegment(sketch, "E276", {"start": v(-19.79, -14.22) * mm, "end": v(-18.9, -14.22) * mm});
            skLineSegment(sketch, "E277", {"start": v(-18.9, -14.22) * mm, "end": v(-18.72, -14.05) * mm});
            skLineSegment(sketch, "E278", {"start": v(-18.72, -14.05) * mm, "end": v(-18.62, -13.8) * mm});
            skLineSegment(sketch, "E279", {"start": v(-18.62, -13.8) * mm, "end": v(-18.68, -13.58) * mm});
            skLineSegment(sketch, "E280", {"start": v(-18.68, -13.58) * mm, "end": v(-18.9, -13.36) * mm});
            skLineSegment(sketch, "E281", {"start": v(-18.9, -13.36) * mm, "end": v(-19.79, -13.36) * mm});
            skLineSegment(sketch, "E282", {"start": v(-19.79, -14.9) * mm, "end": v(-19.79, -15.82) * mm});
            skLineSegment(sketch, "E283", {"start": v(-19.79, -15.82) * mm, "end": v(-18.96, -15.82) * mm});
            skLineSegment(sketch, "E284", {"start": v(-18.96, -15.82) * mm, "end": v(-18.67, -15.7) * mm});
            skLineSegment(sketch, "E285", {"start": v(-18.67, -15.7) * mm, "end": v(-18.59, -15.64) * mm});
            skLineSegment(sketch, "E286", {"start": v(-18.59, -15.64) * mm, "end": v(-18.59, -15.13) * mm});
            skLineSegment(sketch, "E287", {"start": v(-18.59, -15.13) * mm, "end": v(-18.94, -14.94) * mm});
            skLineSegment(sketch, "E288", {"start": v(-18.94, -14.94) * mm, "end": v(-19.26, -14.87) * mm});
            skLineSegment(sketch, "E289", {"start": v(-19.26, -14.87) * mm, "end": v(-19.79, -14.9) * mm});
            skLineSegment(sketch, "E290", {"start": v(-16.06, -13.67) * mm, "end": v(-16.5, -14.51) * mm});
            skLineSegment(sketch, "E291", {"start": v(-16.5, -14.51) * mm, "end": v(-16.1, -15.47) * mm});
            skLineSegment(sketch, "E292", {"start": v(-16.1, -15.47) * mm, "end": v(-15.1, -15.89) * mm});
            skLineSegment(sketch, "E293", {"start": v(-15.1, -15.89) * mm, "end": v(-14.3, -15.5) * mm});
            skLineSegment(sketch, "E294", {"start": v(-14.3, -15.5) * mm, "end": v(-13.91, -14.62) * mm});
            skLineSegment(sketch, "E295", {"start": v(-13.91, -14.62) * mm, "end": v(-14.24, -13.72) * mm});
            skLineSegment(sketch, "E296", {"start": v(-14.24, -13.72) * mm, "end": v(-15.18, -13.36) * mm});
            skLineSegment(sketch, "E297", {"start": v(-15.18, -13.36) * mm, "end": v(-16.06, -13.67) * mm});
            skLineSegment(sketch, "E298", {"start": v(-15.25, -12.73) * mm, "end": v(-16.44, -13.23) * mm});
            skLineSegment(sketch, "E299", {"start": v(-16.44, -13.23) * mm, "end": v(-17.04, -14.55) * mm});
            skLineSegment(sketch, "E300", {"start": v(-17.04, -14.55) * mm, "end": v(-16.54, -15.86) * mm});
            skLineSegment(sketch, "E301", {"start": v(-16.54, -15.86) * mm, "end": v(-15.18, -16.45) * mm});
            skLineSegment(sketch, "E302", {"start": v(-15.18, -16.45) * mm, "end": v(-13.91, -15.95) * mm});
            skLineSegment(sketch, "E303", {"start": v(-13.91, -15.95) * mm, "end": v(-13.22, -14.66) * mm});
            skLineSegment(sketch, "E304", {"start": v(-13.22, -14.66) * mm, "end": v(-13.73, -13.27) * mm});
            skLineSegment(sketch, "E305", {"start": v(-13.73, -13.27) * mm, "end": v(-15.25, -12.73) * mm});
            skLineSegment(sketch, "E306", {"start": v(-12.16, -12.73) * mm, "end": v(-11.75, -12.73) * mm});
            skLineSegment(sketch, "E307", {"start": v(-11.75, -12.73) * mm, "end": v(-9.7, -15.29) * mm});
            skLineSegment(sketch, "E308", {"start": v(-9.7, -15.29) * mm, "end": v(-9.7, -12.73) * mm});
            skLineSegment(sketch, "E309", {"start": v(-9.7, -12.73) * mm, "end": v(-9.12, -12.73) * mm});
            skLineSegment(sketch, "E310", {"start": v(-9.12, -12.73) * mm, "end": v(-9.12, -16.46) * mm});
            skLineSegment(sketch, "E311", {"start": v(-9.12, -16.46) * mm, "end": v(-9.51, -16.46) * mm});
            skLineSegment(sketch, "E312", {"start": v(-9.51, -16.46) * mm, "end": v(-11.58, -13.83) * mm});
            skLineSegment(sketch, "E313", {"start": v(-11.58, -13.83) * mm, "end": v(-11.58, -16.4) * mm});
            skLineSegment(sketch, "E314", {"start": v(-11.58, -16.4) * mm, "end": v(-12.16, -16.4) * mm});
            skLineSegment(sketch, "E315", {"start": v(-12.16, -16.4) * mm, "end": v(-12.16, -12.73) * mm});
            skLineSegment(sketch, "E316", {"start": v(-7.8, -12.73) * mm, "end": v(-7.8, -16.44) * mm});
            skLineSegment(sketch, "E317", {"start": v(-7.8, -16.44) * mm, "end": v(-5.56, -16.44) * mm});
            skLineSegment(sketch, "E318", {"start": v(-5.56, -16.44) * mm, "end": v(-5.56, -15.93) * mm});
            skLineSegment(sketch, "E319", {"start": v(-5.56, -15.93) * mm, "end": v(-7.22, -15.93) * mm});
            skLineSegment(sketch, "E320", {"start": v(-7.22, -15.93) * mm, "end": v(-7.22, -14.84) * mm});
            skLineSegment(sketch, "E321", {"start": v(-7.22, -14.84) * mm, "end": v(-5.72, -14.84) * mm});
            skLineSegment(sketch, "E322", {"start": v(-5.72, -14.84) * mm, "end": v(-5.72, -14.3) * mm});
            skLineSegment(sketch, "E323", {"start": v(-5.72, -14.3) * mm, "end": v(-7.22, -14.3) * mm});
            skLineSegment(sketch, "E324", {"start": v(-7.22, -14.3) * mm, "end": v(-7.22, -13.28) * mm});
            skLineSegment(sketch, "E325", {"start": v(-7.22, -13.28) * mm, "end": v(-5.72, -13.28) * mm});
            skLineSegment(sketch, "E326", {"start": v(-7.8, -12.73) * mm, "end": v(-5.72, -12.73) * mm});
            skLineSegment(sketch, "E327", {"start": v(-5.72, -12.73) * mm, "end": v(-5.72, -13.28) * mm});
            skLineSegment(sketch, "E328", {"start": v(-2.81, -12.73) * mm, "end": v(-2.81, -16.35) * mm});
            skLineSegment(sketch, "E329", {"start": v(-2.81, -16.35) * mm, "end": v(-1.02, -16.35) * mm});
            skLineSegment(sketch, "E330", {"start": v(-1.02, -16.35) * mm, "end": v(-0.4, -15.64) * mm});
            skLineSegment(sketch, "E331", {"start": v(-0.4, -15.64) * mm, "end": v(-0.48, -14.9) * mm});
            skLineSegment(sketch, "E332", {"start": v(-0.48, -14.9) * mm, "end": v(-0.99, -14.58) * mm});
            skLineSegment(sketch, "E333", {"start": v(-0.99, -14.58) * mm, "end": v(-0.4, -13.65) * mm});
            skLineSegment(sketch, "E334", {"start": v(-0.4, -13.65) * mm, "end": v(-1.02, -12.92) * mm});
            skLineSegment(sketch, "E335", {"start": v(-1.02, -12.92) * mm, "end": v(-1.44, -12.73) * mm});
            skLineSegment(sketch, "E336", {"start": v(-1.44, -12.73) * mm, "end": v(-2.81, -12.73) * mm});
            skLineSegment(sketch, "E337", {"start": v(-2.3, -13.28) * mm, "end": v(-2.3, -14.24) * mm});
            skLineSegment(sketch, "E338", {"start": v(-2.3, -14.24) * mm, "end": v(-1.3, -14.24) * mm});
            skLineSegment(sketch, "E339", {"start": v(-1.3, -14.24) * mm, "end": v(-1.07, -13.8) * mm});
            skLineSegment(sketch, "E340", {"start": v(-1.07, -13.8) * mm, "end": v(-1.4, -13.28) * mm});
            skLineSegment(sketch, "E341", {"start": v(-1.4, -13.28) * mm, "end": v(-2.3, -13.28) * mm});
            skLineSegment(sketch, "E342", {"start": v(-2.3, -14.85) * mm, "end": v(-2.3, -15.73) * mm});
            skLineSegment(sketch, "E343", {"start": v(-2.3, -15.73) * mm, "end": v(-2.1, -15.9) * mm});
            skLineSegment(sketch, "E344", {"start": v(-2.1, -15.9) * mm, "end": v(-1.5, -15.9) * mm});
            skLineSegment(sketch, "E345", {"start": v(-1.5, -15.9) * mm, "end": v(-1.09, -15.68) * mm});
            skLineSegment(sketch, "E346", {"start": v(-1.09, -15.68) * mm, "end": v(-1.09, -15.16) * mm});
            skLineSegment(sketch, "E347", {"start": v(-1.09, -15.16) * mm, "end": v(-1.95, -14.84) * mm});
            skLineSegment(sketch, "E348", {"start": v(-1.95, -14.84) * mm, "end": v(-2.3, -14.85) * mm});
            skLineSegment(sketch, "E349", {"start": v(0.9, -12.8) * mm, "end": v(0.9, -16.27) * mm});
            skLineSegment(sketch, "E350", {"start": v(0.9, -16.27) * mm, "end": v(1.34, -16.27) * mm});
            skLineSegment(sketch, "E351", {"start": v(1.34, -16.27) * mm, "end": v(1.34, -14.98) * mm});
            skLineSegment(sketch, "E352", {"start": v(1.34, -14.98) * mm, "end": v(2.14, -14.98) * mm});
            skLineSegment(sketch, "E353", {"start": v(2.14, -14.98) * mm, "end": v(2.83, -16.41) * mm});
            skLineSegment(sketch, "E354", {"start": v(2.83, -16.41) * mm, "end": v(3.35, -16.16) * mm});
            skLineSegment(sketch, "E355", {"start": v(3.35, -16.16) * mm, "end": v(2.73, -14.85) * mm});
            skLineSegment(sketch, "E356", {"start": v(2.73, -14.85) * mm, "end": v(3.39, -13.96) * mm});
            skLineSegment(sketch, "E357", {"start": v(3.39, -13.96) * mm, "end": v(3.1, -13.12) * mm});
            skLineSegment(sketch, "E358", {"start": v(3.1, -13.12) * mm, "end": v(2.4, -12.75) * mm});
            skLineSegment(sketch, "E359", {"start": v(2.4, -12.75) * mm, "end": v(0.9, -12.8) * mm});
            skLineSegment(sketch, "E360", {"start": v(1.41, -13.39) * mm, "end": v(1.41, -14.37) * mm});
            skLineSegment(sketch, "E361", {"start": v(1.41, -14.37) * mm, "end": v(1.63, -14.56) * mm});
            skLineSegment(sketch, "E362", {"start": v(1.63, -14.56) * mm, "end": v(2.2, -14.56) * mm});
            skLineSegment(sketch, "E363", {"start": v(2.2, -14.56) * mm, "end": v(2.62, -14.28) * mm});
            skLineSegment(sketch, "E364", {"start": v(2.62, -14.28) * mm, "end": v(2.7, -14.23) * mm});
            skLineSegment(sketch, "E365", {"start": v(2.7, -14.23) * mm, "end": v(2.7, -13.68) * mm});
            skLineSegment(sketch, "E366", {"start": v(2.7, -13.68) * mm, "end": v(2.37, -13.35) * mm});
            skLineSegment(sketch, "E367", {"start": v(2.37, -13.35) * mm, "end": v(1.5, -13.35) * mm});
            skLineSegment(sketch, "E368", {"start": v(1.5, -13.35) * mm, "end": v(1.41, -13.39) * mm});
            skLineSegment(sketch, "E369", {"start": v(6.2, -13.26) * mm, "end": v(5.28, -13.62) * mm});
            skLineSegment(sketch, "E370", {"start": v(5.28, -13.62) * mm, "end": v(4.87, -14.62) * mm});
            skLineSegment(sketch, "E371", {"start": v(4.87, -14.62) * mm, "end": v(5.23, -15.45) * mm});
            skLineSegment(sketch, "E372", {"start": v(5.23, -15.45) * mm, "end": v(6.13, -15.88) * mm});
            skLineSegment(sketch, "E373", {"start": v(6.13, -15.88) * mm, "end": v(7.11, -15.5) * mm});
            skLineSegment(sketch, "E374", {"start": v(7.11, -15.5) * mm, "end": v(7.47, -14.69) * mm});
            skLineSegment(sketch, "E375", {"start": v(7.47, -14.69) * mm, "end": v(7.15, -13.73) * mm});
            skLineSegment(sketch, "E376", {"start": v(7.15, -13.73) * mm, "end": v(6.2, -13.26) * mm});
            skLineSegment(sketch, "E377", {"start": v(6.2, -12.7) * mm, "end": v(4.85, -13.26) * mm});
            skLineSegment(sketch, "E378", {"start": v(4.85, -13.26) * mm, "end": v(4.31, -14.59) * mm});
            skLineSegment(sketch, "E379", {"start": v(4.31, -14.59) * mm, "end": v(4.89, -15.91) * mm});
            skLineSegment(sketch, "E380", {"start": v(4.89, -15.91) * mm, "end": v(6.1, -16.52) * mm});
            skLineSegment(sketch, "E381", {"start": v(6.1, -16.52) * mm, "end": v(7.51, -15.94) * mm});
            skLineSegment(sketch, "E382", {"start": v(7.51, -15.94) * mm, "end": v(8.05, -14.65) * mm});
            skLineSegment(sketch, "E383", {"start": v(8.05, -14.65) * mm, "end": v(7.56, -13.26) * mm});
            skLineSegment(sketch, "E384", {"start": v(7.56, -13.26) * mm, "end": v(6.2, -12.7) * mm});
            skLineSegment(sketch, "E385", {"start": v(8.52, -12.7) * mm, "end": v(8.52, -13.26) * mm});
            skLineSegment(sketch, "E386", {"start": v(8.52, -13.26) * mm, "end": v(9.49, -13.26) * mm});
            skLineSegment(sketch, "E387", {"start": v(9.49, -13.26) * mm, "end": v(9.49, -16.33) * mm});
            skLineSegment(sketch, "E388", {"start": v(9.49, -16.33) * mm, "end": v(10.12, -16.33) * mm});
            skLineSegment(sketch, "E389", {"start": v(10.12, -16.33) * mm, "end": v(10.12, -13.26) * mm});
            skLineSegment(sketch, "E390", {"start": v(10.12, -13.26) * mm, "end": v(11, -13.26) * mm});
            skLineSegment(sketch, "E391", {"start": v(11, -13.26) * mm, "end": v(11, -12.7) * mm});
            skLineSegment(sketch, "E392", {"start": v(11, -12.7) * mm, "end": v(8.52, -12.7) * mm});
            skLineSegment(sketch, "E393", {"start": v(11.93, -12.8) * mm, "end": v(12.53, -12.8) * mm});
            skLineSegment(sketch, "E394", {"start": v(12.53, -12.8) * mm, "end": v(12.53, -14.3) * mm});
            skLineSegment(sketch, "E395", {"start": v(12.53, -14.3) * mm, "end": v(14.2, -14.3) * mm});
            skLineSegment(sketch, "E396", {"start": v(14.2, -14.3) * mm, "end": v(14.2, -12.8) * mm});
            skLineSegment(sketch, "E397", {"start": v(14.2, -12.8) * mm, "end": v(14.87, -12.8) * mm});
            skLineSegment(sketch, "E398", {"start": v(14.87, -12.8) * mm, "end": v(14.87, -16.37) * mm});
            skLineSegment(sketch, "E399", {"start": v(14.87, -16.37) * mm, "end": v(14.25, -16.37) * mm});
            skLineSegment(sketch, "E400", {"start": v(14.25, -16.37) * mm, "end": v(14.25, -14.84) * mm});
            skLineSegment(sketch, "E401", {"start": v(14.25, -14.84) * mm, "end": v(12.51, -14.84) * mm});
            skLineSegment(sketch, "E402", {"start": v(12.51, -14.84) * mm, "end": v(12.51, -16.4) * mm});
            skLineSegment(sketch, "E403", {"start": v(12.51, -16.4) * mm, "end": v(11.93, -16.4) * mm});
            skLineSegment(sketch, "E404", {"start": v(11.93, -16.4) * mm, "end": v(11.93, -12.8) * mm});
            skSolve(sketch);
        }
        {
            var Q0;
            Q0=makeQuery(id+"F0.imprint","IMPRINT",FACE,{"disambiguationData":[TD([[makeQuery(id+"F0.imprint","IMPRINT",EDGE,{"derivedFrom":sQuery(id+"F0.wireOp",EDGE,"E4")}),1.0]])]});
            var Q1;
            Q1=makeQuery(id+"F0.imprint","IMPRINT",FACE,{"disambiguationData":[TD([[makeQuery(id+"F0.imprint","IMPRINT",EDGE,{"derivedFrom":sQuery(id+"F0.wireOp",EDGE,"E19")}),1.0]])]});
            var Q2;
            Q2=makeQuery(id+"F0.imprint","IMPRINT",FACE,{"disambiguationData":[TD([[makeQuery(id+"F0.imprint","IMPRINT",EDGE,{"derivedFrom":sQuery(id+"F0.wireOp",EDGE,"E32")}),1.0]])]});
            var Q3;
            Q3=makeQuery(id+"F0.imprint","IMPRINT",FACE,{"disambiguationData":[TD([[makeQuery(id+"F0.imprint","IMPRINT",EDGE,{"derivedFrom":sQuery(id+"F0.wireOp",EDGE,"E44")}),1.0]])]});
            var Q4;
            Q4=makeQuery(id+"F0.imprint","IMPRINT",FACE,{"disambiguationData":[TD([[makeQuery(id+"F0.imprint","IMPRINT",EDGE,{"derivedFrom":sQuery(id+"F0.wireOp",EDGE,"E8")}),1.0]])]});
            var Q5;
            Q5=makeQuery(id+"F1.imprint","IMPRINT",FACE,{"disambiguationData":[TD([[makeQuery(id+"F1.imprint","IMPRINT",EDGE,{"derivedFrom":sQuery(id+"F1.wireOp",EDGE,"E210")}),-1.0]])]});
            var Q6;
            Q6=makeQuery(id+"F1.imprint","IMPRINT",FACE,{"disambiguationData":[TD([[makeQuery(id+"F1.imprint","IMPRINT",EDGE,{"derivedFrom":sQuery(id+"F1.wireOp",EDGE,"E116")}),-1.0]])]});
            var Q7;
            Q7=makeQuery(id+"F1.imprint","IMPRINT",FACE,{"disambiguationData":[TD([[makeQuery(id+"F1.imprint","IMPRINT",EDGE,{"derivedFrom":sQuery(id+"F1.wireOp",EDGE,"E229")}),1.0]])]});
            var Q8;
            Q8=makeQuery(id+"F1.imprint","IMPRINT",FACE,{"disambiguationData":[TD([[makeQuery(id+"F1.imprint","IMPRINT",EDGE,{"derivedFrom":sQuery(id+"F1.wireOp",EDGE,"E369")}),-1.0]])]});
            var Q9;
            Q9=makeQuery(id+"F1.imprint","IMPRINT",FACE,{"disambiguationData":[TD([[makeQuery(id+"F1.imprint","IMPRINT",EDGE,{"derivedFrom":sQuery(id+"F1.wireOp",EDGE,"E349")}),1.0]])]});
            var Q10;
            Q10=makeQuery(id+"F1.imprint","IMPRINT",FACE,{"disambiguationData":[TD([[makeQuery(id+"F1.imprint","IMPRINT",EDGE,{"derivedFrom":sQuery(id+"F1.wireOp",EDGE,"E191")}),1.0]])]});
            var Q11;
            Q11=makeQuery(id+"F1.imprint","IMPRINT",FACE,{"disambiguationData":[TD([[makeQuery(id+"F1.imprint","IMPRINT",EDGE,{"derivedFrom":sQuery(id+"F1.wireOp",EDGE,"E167")}),-1.0]])]});
            var Q12;
            Q12=makeQuery(id+"F1.imprint","IMPRINT",FACE,{"disambiguationData":[TD([[makeQuery(id+"F1.imprint","IMPRINT",EDGE,{"derivedFrom":sQuery(id+"F1.wireOp",EDGE,"E253")}),-1.0]])]});
            var Q13;
            Q13=makeQuery(id+"F1.imprint","IMPRINT",FACE,{"disambiguationData":[TD([[makeQuery(id+"F1.imprint","IMPRINT",EDGE,{"derivedFrom":sQuery(id+"F1.wireOp",EDGE,"E306")}),-1.0]])]});
            var Q14;
            Q14=makeQuery(id+"F1.imprint","IMPRINT",FACE,{"disambiguationData":[TD([[makeQuery(id+"F1.imprint","IMPRINT",EDGE,{"derivedFrom":sQuery(id+"F1.wireOp",EDGE,"E316")}),1.0]])]});
            var Q15;
            Q15=makeQuery(id+"F1.imprint","IMPRINT",FACE,{"disambiguationData":[TD([[makeQuery(id+"F1.imprint","IMPRINT",EDGE,{"derivedFrom":sQuery(id+"F1.wireOp",EDGE,"E385")}),1.0]])]});
            var Q16;
            Q16=makeQuery(id+"F1.imprint","IMPRINT",FACE,{"disambiguationData":[TD([[makeQuery(id+"F1.imprint","IMPRINT",EDGE,{"derivedFrom":sQuery(id+"F1.wireOp",EDGE,"E393")}),-1.0]])]});
            var Q17;
            Q17=makeQuery(id+"F1.imprint","IMPRINT",FACE,{"disambiguationData":[TD([[makeQuery(id+"F1.imprint","IMPRINT",EDGE,{"derivedFrom":sQuery(id+"F1.wireOp",EDGE,"E57")}),1.0]])]});
            var Q18;
            Q18=makeQuery(id+"F1.imprint","IMPRINT",FACE,{"disambiguationData":[TD([[makeQuery(id+"F1.imprint","IMPRINT",EDGE,{"derivedFrom":sQuery(id+"F1.wireOp",EDGE,"E85")}),-1.0]])]});
            var Q19;
            Q19=makeQuery(id+"F1.imprint","IMPRINT",FACE,{"disambiguationData":[TD([[makeQuery(id+"F1.imprint","IMPRINT",EDGE,{"derivedFrom":sQuery(id+"F1.wireOp",EDGE,"E180")}),1.0]])]});
            var Q20;
            Q20=makeQuery(id+"F1.imprint","IMPRINT",FACE,{"disambiguationData":[TD([[makeQuery(id+"F1.imprint","IMPRINT",EDGE,{"derivedFrom":sQuery(id+"F1.wireOp",EDGE,"E267")}),1.0]])]});
            var Q21;
            Q21=makeQuery(id+"F1.imprint","IMPRINT",FACE,{"disambiguationData":[TD([[makeQuery(id+"F1.imprint","IMPRINT",EDGE,{"derivedFrom":sQuery(id+"F1.wireOp",EDGE,"E290")}),-1.0]])]});
            var Q22;
            Q22=makeQuery(id+"F1.imprint","IMPRINT",FACE,{"disambiguationData":[TD([[makeQuery(id+"F1.imprint","IMPRINT",EDGE,{"derivedFrom":sQuery(id+"F1.wireOp",EDGE,"E328")}),1.0]])]});
            extrude(context, id + "F2", {"entities" : qUnion([Q0, Q1, Q2, Q3, Q4, Q5, Q6, Q7, Q8, Q9, Q10, Q11, Q12, Q13, Q14, Q15, Q16, Q17, Q18, Q19, Q20, Q21, Q22]), "depth" : 10 * mm});
        }
        {
            var Q0;
            Q0=qCreatedBy(makeId("Front.planeOp"),FACE);
            var sketch = newSketch(context, id + "F3", { "sketchPlane" : qUnion([Q0])});
            skLineSegment(sketch, "E405.bottom", {"start": v(-34.63, 18.8) * mm, "end": v(34.63, 18.8) * mm});
            skLineSegment(sketch, "E405.top", {"start": v(-34.63, -19.35) * mm, "end": v(34.63, -19.35) * mm});
            skLineSegment(sketch, "E405.left", {"start": v(-34.63, 18.8) * mm, "end": v(-34.63, -19.35) * mm});
            skLineSegment(sketch, "E405.right", {"start": v(34.63, 18.8) * mm, "end": v(34.63, -19.35) * mm});
            skSolve(sketch);
        }
        {
            var Q0;
            Q0=makeQuery(id+"F3.imprint","IMPRINT",FACE,{"disambiguationData":[TD([[makeQuery(id+"F3.imprint","IMPRINT",EDGE,{"derivedFrom":sQuery(id+"F3.wireOp",EDGE,"E405.bottom")}),-1.0]])]});
            extrude(context, id + "F4", {"entities" : qUnion([Q0]), "depth" : 5 * mm});
        }
    });
